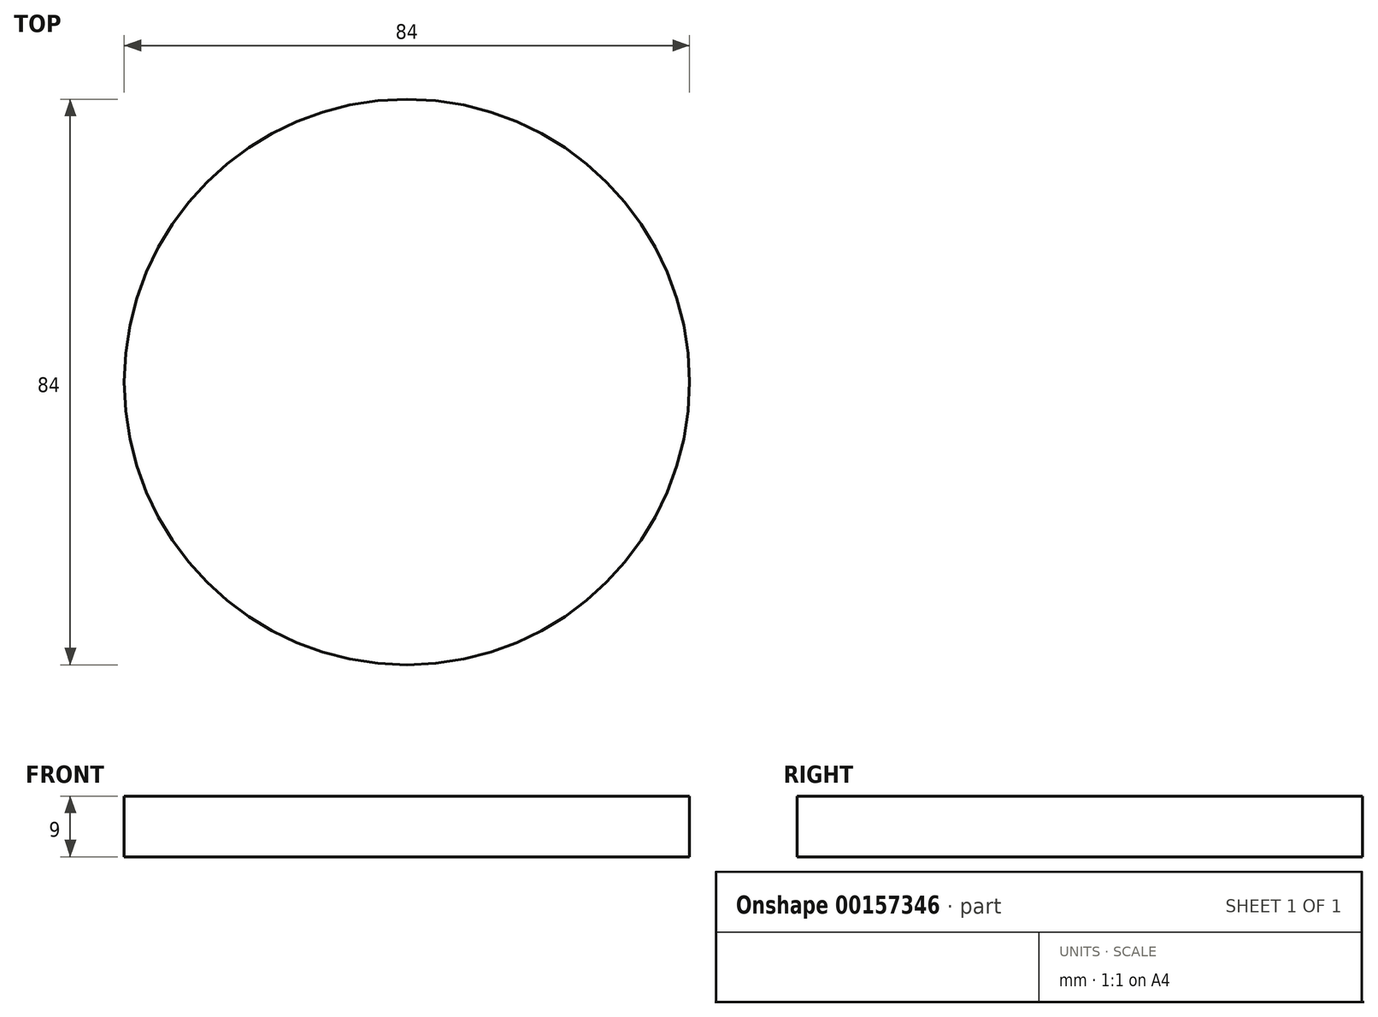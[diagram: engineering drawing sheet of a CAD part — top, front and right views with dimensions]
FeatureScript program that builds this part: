
annotation { "Feature Type Name" : "Feature", "Feature Type Description" : "" }
export const myFeature = defineFeature(function(context is Context, id is Id, definition is map)
    precondition{}
    {
        {
            var Q0;
            Q0=qCreatedBy(makeId("Top.planeOp"),FACE);
            var sketch = newSketch(context, id + "F0", { "sketchPlane" : qUnion([Q0])});
            skCircle(sketch, "E0", {"center": v(0, 0) * mm, "radius": 42 * mm});
            skSolve(sketch);
        }
        {
            var Q0;
            Q0=makeQuery(id+"F0.imprint","IMPRINT",FACE,{"disambiguationData":[TD([[makeQuery(id+"F0.imprint","IMPRINT",EDGE,{"derivedFrom":sQuery(id+"F0.wireOp",EDGE,"E0")}),1.0]])]});
            extrude(context, id + "F1", {"entities" : qUnion([Q0]), "depth" : 9 * mm});
        }
    });
